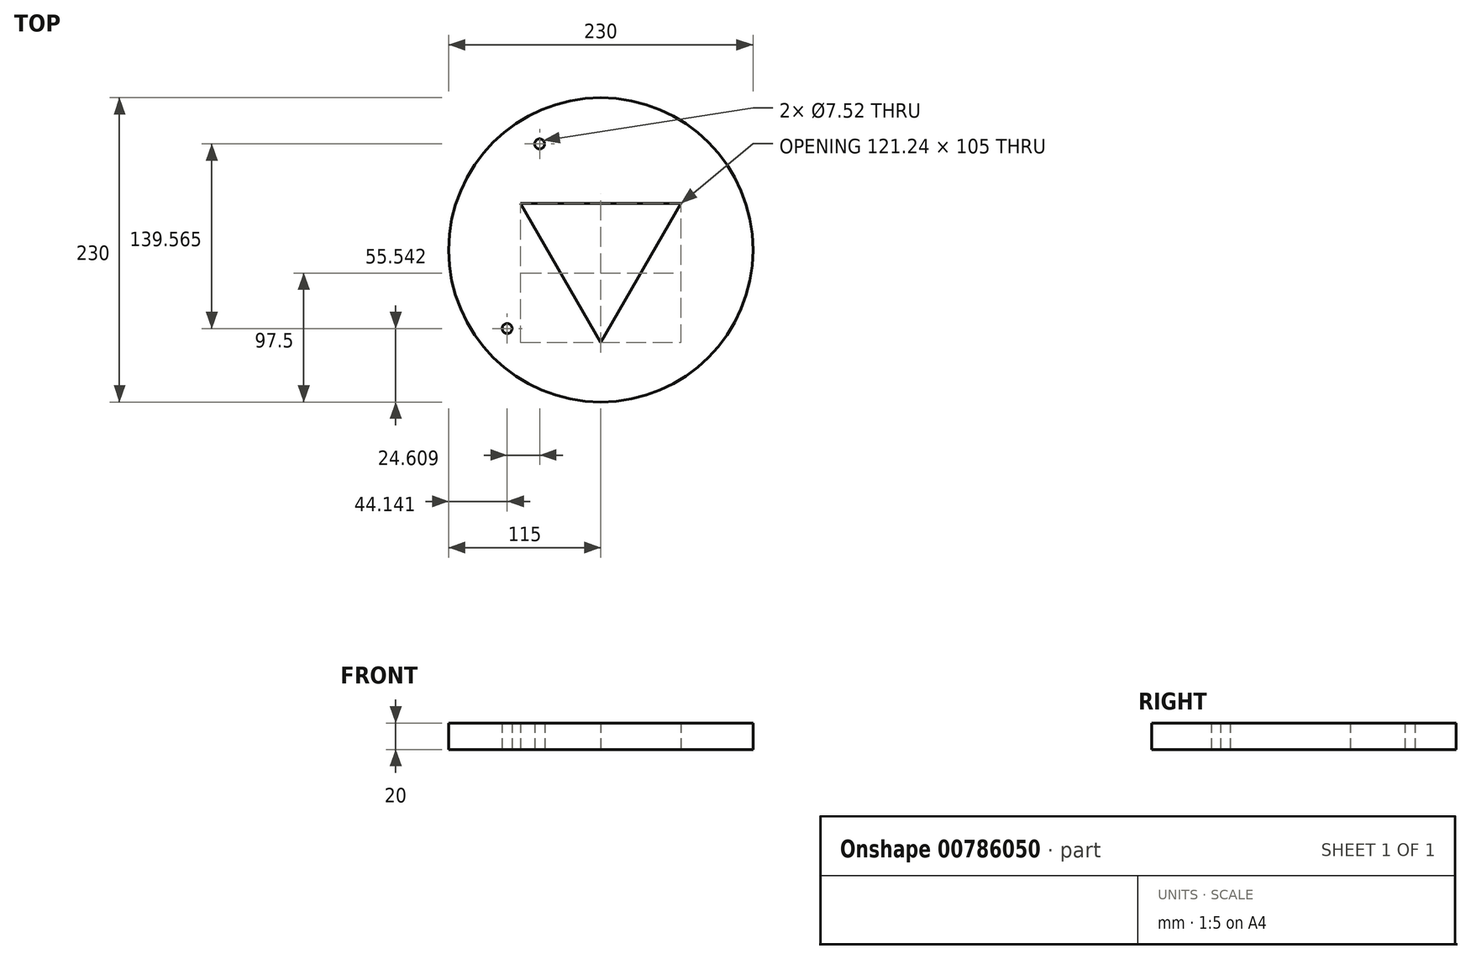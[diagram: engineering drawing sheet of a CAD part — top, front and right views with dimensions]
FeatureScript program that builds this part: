
annotation { "Feature Type Name" : "Feature", "Feature Type Description" : "" }
export const myFeature = defineFeature(function(context is Context, id is Id, definition is map)
    precondition{}
    {
        {
            var Q0;
            Q0=qCreatedBy(makeId("Top.planeOp"),FACE);
            var sketch = newSketch(context, id + "F0", { "sketchPlane" : qUnion([Q0])});
            skCircle(sketch, "E0", {"center": v(0, 0) * mm, "radius": 115 * mm});
            skCircle(sketch, "E1", {"center": v(0, 0) * mm, "radius": 15 * mm});
            skCircle(sketch, "E2.cCircle", {"center": v(0, 0) * mm, "radius": 35 * mm, "construction": true});
            skLineSegment(sketch, "E2.0", {"start": v(-60.62, 35) * mm, "end": v(60.62, 35) * mm});
            skLineSegment(sketch, "E2.1", {"start": v(60.62, 35) * mm, "end": v(0, -70) * mm});
            skLineSegment(sketch, "E2.2", {"start": v(0, -70) * mm, "end": v(-60.62, 35) * mm});
            skPoint(sketch, "E2.0.midPoint", {"position": v(0, 35) * mm});
            skSolve(sketch);
        }
        {
            var Q0;
            Q0=qSketchRegion(id+"F0",true);
            extrude(context, id + "F1", {"entities" : qUnion([Q0]), "depth" : 20 * mm});
        }
        {
            var Q0;
            Q0=makeQuery(id+"F1.opExtrude","CAP_FACE",FACE,{"disambiguationData":[OSD([sQuery(id+"F0.wireOp",EDGE,"E0"),sQuery(id+"F0.wireOp",EDGE,"E2.0"),sQuery(id+"F0.wireOp",EDGE,"E2.1"),sQuery(id+"F0.wireOp",EDGE,"E2.2")])],"isStart":true});
            var sketch = newSketch(context, id + "F2", { "sketchPlane" : qUnion([Q0])});
            skCircle(sketch, "E3", {"center": v(0, 0) * mm, "radius": 92.5 * mm, "construction": true});
            skCircle(sketch, "E4", {"center": v(-70.86, 59.46) * mm, "radius": 3.76 * mm});
            skCircle(sketch, "E5", {"center": v(-46.25, -80.1) * mm, "radius": 3.76 * mm});
            skLineSegment(sketch, "E6", {"start": v(-70.86, 59.46) * mm, "end": v(0, 0) * mm, "construction": true});
            skLineSegment(sketch, "E7", {"start": v(0, 0) * mm, "end": v(-46.25, -80.1) * mm, "construction": true});
            skLineSegment(sketch, "E8", {"start": v(0, 0) * mm, "end": v(-92.5, 0) * mm, "construction": true});
            skLineSegment(sketch, "E9", {"start": v(0, 92.5) * mm, "end": v(0, -92.5) * mm, "construction": true});
            skCircle(sketch, "E10", {"center": v(92.5, 0) * mm, "radius": 3.76 * mm, "construction": true});
            skSolve(sketch);
        }
        {
            var Q0;
            Q0=qSketchRegion(id+"F2",true);
            extrude(context, id + "F3", {"entities" : qUnion([Q0]), "operationType" : NewBodyOperationType.REMOVE, "oppositeDirection" : true, "depth" : 25 * mm, "offsetDistance" : 25 * mm});
        }
    });
